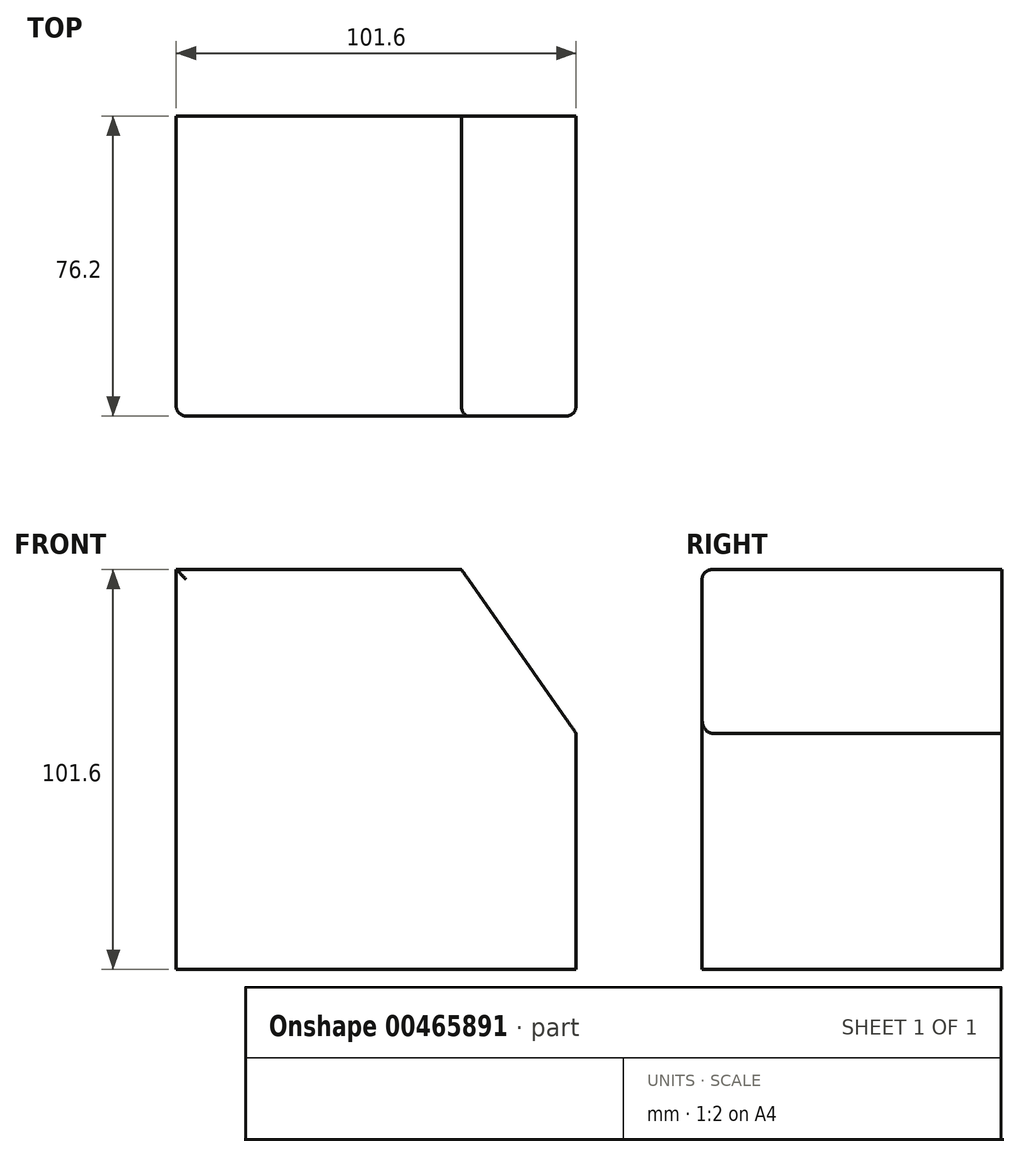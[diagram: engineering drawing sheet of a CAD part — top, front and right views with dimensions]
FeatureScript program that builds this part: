
annotation { "Feature Type Name" : "Feature", "Feature Type Description" : "" }
export const myFeature = defineFeature(function(context is Context, id is Id, definition is map)
    precondition{}
    {
        {
            var Q0;
            Q0=qCreatedBy(makeId("Front.planeOp"),FACE);
            var sketch = newSketch(context, id + "F0", { "sketchPlane" : qUnion([Q0])});
            skPoint(sketch, "E0.middle", {"position": v(0, 0) * mm});
            skLineSegment(sketch, "E1.bottom", {"start": v(-50.8, 50.8) * mm, "end": v(50.8, 50.8) * mm});
            skLineSegment(sketch, "E1.top", {"start": v(-50.8, -50.8) * mm, "end": v(50.8, -50.8) * mm});
            skLineSegment(sketch, "E1.left", {"start": v(-50.8, 50.8) * mm, "end": v(-50.8, -50.8) * mm});
            skLineSegment(sketch, "E1.right", {"start": v(50.8, 50.8) * mm, "end": v(50.8, -50.8) * mm});
            skLineSegment(sketch, "E2", {"start": v(21.66, 50.8) * mm, "end": v(50.8, 9.19) * mm});
            skSolve(sketch);
        }
        {
            var Q0;
            {var subQ1=sQuery(id+"F0.wireOp",EDGE,"E1.top");Q0=makeQuery(id+"F0.imprint","IMPRINT",FACE,{"disambiguationData":[TD([[makeQuery(id+"F0.imprint","IMPRINT",EDGE,{"derivedFrom":subQ1}),1.0]])]});}
            extrude(context, id + "F1", {"entities" : qUnion([Q0]), "endBound" : BoundingType.SYMMETRIC, "depth" : 76.2 * mm, "offsetDistance" : 25.4 * mm});
        }
        {
            var Q0;
            Q0=makeQuery(id+"F1.opExtrude","CAP_EDGE",EDGE,{"disambiguationData":[OSD([sQuery(id+"F0.wireOp",EDGE,"E1.left")])],"isStart":false});
            var Q1;
            Q1=makeQuery(id+"F1.opExtrude","CAP_EDGE",EDGE,{"disambiguationData":[OSD([sQuery(id+"F0.wireOp",EDGE,"E1.bottom")])],"isStart":false});
            fillet(context, id + "F2", {"entities" : qUnion([Q0, Q1]), "radius" : 2.54 * mm, "tangentPropagation" : true, "allowEdgeOverflow" : false});
        }
        {
            var Q0;
            Q0=makeQuery(id+"F1.opExtrude","CAP_EDGE",EDGE,{"disambiguationData":[OSD([sQuery(id+"F0.wireOp",EDGE,"E1.right")])],"isStart":false});
            fillet(context, id + "F3", {"entities" : qUnion([Q0]), "radius" : 2.54 * mm, "tangentPropagation" : true, "allowEdgeOverflow" : false});
        }
    });
